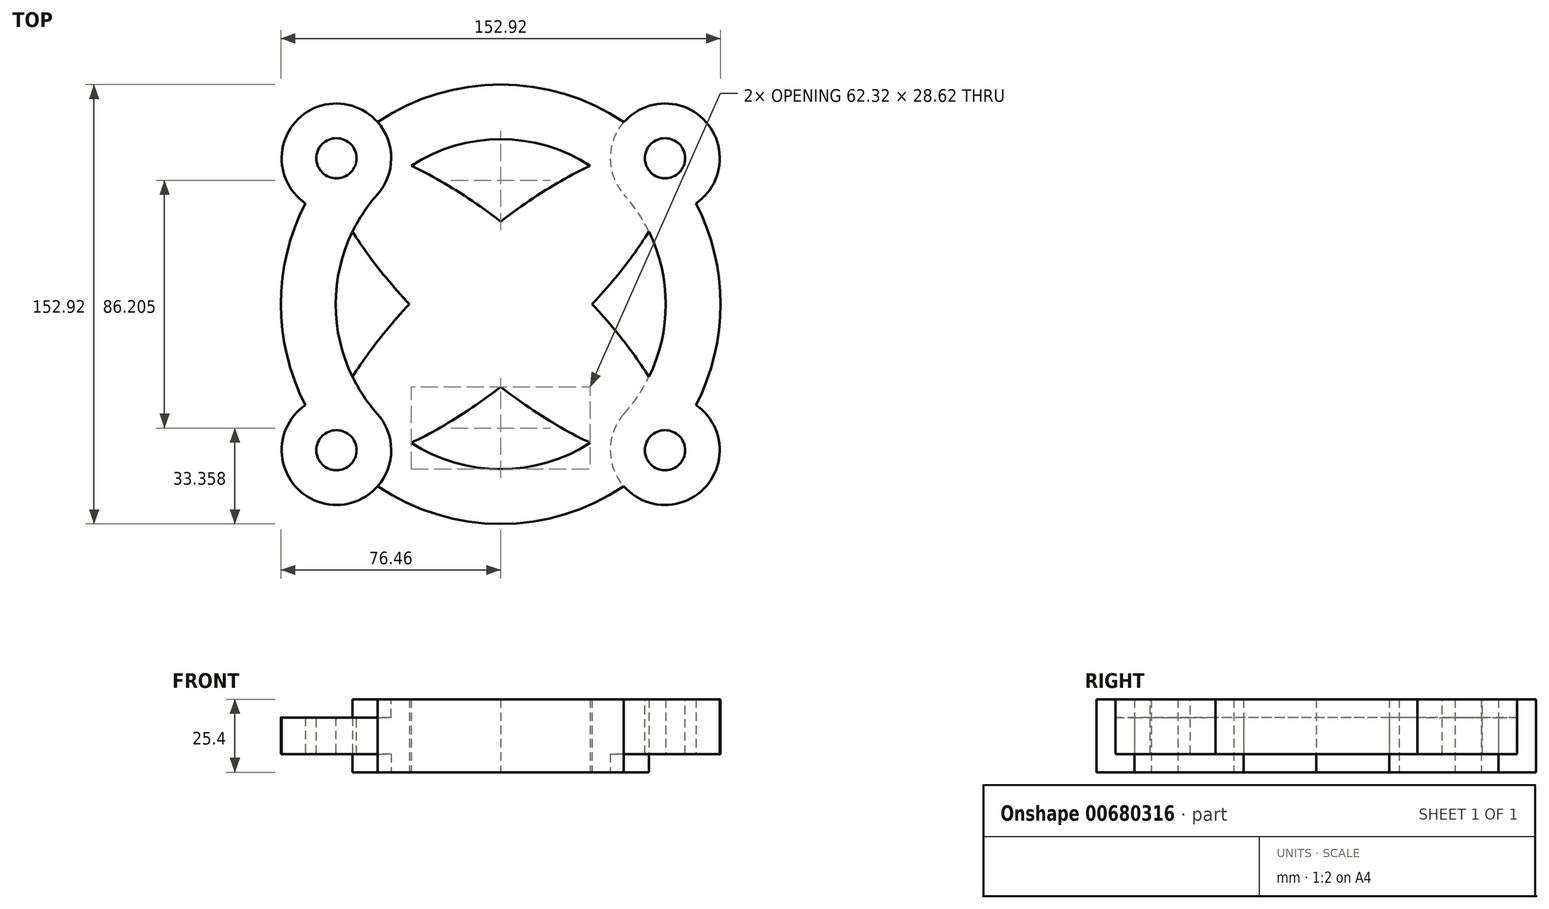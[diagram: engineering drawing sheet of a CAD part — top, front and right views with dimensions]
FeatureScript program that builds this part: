
annotation { "Feature Type Name" : "Feature", "Feature Type Description" : "" }
export const myFeature = defineFeature(function(context is Context, id is Id, definition is map)
    precondition{}
    {
        {
            var Q0;
            Q0=qCreatedBy(makeId("Top.planeOp"),FACE);
            var sketch = newSketch(context, id + "F0", { "sketchPlane" : qUnion([Q0])});
            skLineSegment(sketch, "E0.bottom", {"start": v(76.2, 69.85) * mm, "end": v(-76.2, 69.85) * mm, "construction": true});
            skLineSegment(sketch, "E0.top", {"start": v(76.2, -69.85) * mm, "end": v(-76.2, -69.85) * mm, "construction": true});
            skLineSegment(sketch, "E0.left", {"start": v(76.2, 69.85) * mm, "end": v(76.2, -69.85) * mm, "construction": true});
            skLineSegment(sketch, "E0.right", {"start": v(-76.2, 69.85) * mm, "end": v(-76.2, -69.85) * mm, "construction": true});
            skPoint(sketch, "E0.middle", {"position": v(0, 0) * mm});
            skCircle(sketch, "E1", {"center": v(57.15, 50.8) * mm, "radius": 19.05 * mm});
            skCircle(sketch, "E2", {"center": v(-57.15, 50.8) * mm, "radius": 19.05 * mm});
            skCircle(sketch, "E3", {"center": v(57.15, -50.8) * mm, "radius": 19.05 * mm});
            skCircle(sketch, "E4", {"center": v(-57.15, -50.8) * mm, "radius": 19.05 * mm});
            skEllipse(sketch, "E5", {"center": v(0, 0) * mm, "majorRadius": 76.46 * mm, "minorRadius": 22.23 * mm, "majorAxis": v(0.75, 0.66)});
            skEllipse(sketch, "E6", {"center": v(0, 0) * mm, "majorRadius": 76.46 * mm, "minorRadius": 22.23 * mm, "majorAxis": v(0.75, -0.66)});
            skLineSegment(sketch, "E7", {"start": v(-57.15, 50.8) * mm, "end": v(57.15, -50.8) * mm, "construction": true});
            skLineSegment(sketch, "E8", {"start": v(57.15, 50.8) * mm, "end": v(-57.15, -50.8) * mm, "construction": true});
            skCircle(sketch, "E9", {"center": v(0, 0) * mm, "radius": 76.46 * mm});
            skCircle(sketch, "E10", {"center": v(0, 0) * mm, "radius": 57.41 * mm});
            skSolve(sketch);
        }
        {
            var Q0;
            {var subQ0=sQuery(id+"F0.wireOp",EDGE,"E9");var subQ1=sQuery(id+"F0.wireOp",EDGE,"E2");var subQ2=makeQuery(id+"F0.imprint","INTERSECT",VERTEX,{"disambiguationData":[OD(0.0)],"derivedFrom":[subQ1,subQ0]});Q0=makeQuery(id+"F0.imprint","IMPRINT",FACE,{"disambiguationData":[TD([[makeQuery(id+"F0.imprint","IMPRINT",EDGE,{"disambiguationData":[TD([[subQ2,-1.0]])],"derivedFrom":subQ1}),1.0]])]});}
            var Q1;
            {var subQ5=sQuery(id+"F0.wireOp",EDGE,"E9");var subQ6=sQuery(id+"F0.wireOp",EDGE,"E1");var subQ7=makeQuery(id+"F0.imprint","INTERSECT",VERTEX,{"disambiguationData":[OD(0.0)],"derivedFrom":[subQ6,subQ5]});Q1=makeQuery(id+"F0.imprint","IMPRINT",FACE,{"disambiguationData":[TD([[makeQuery(id+"F0.imprint","IMPRINT",EDGE,{"disambiguationData":[TD([[subQ7,-1.0]])],"derivedFrom":subQ6}),-1.0]])]});}
            var Q2;
            {var subQ0=sQuery(id+"F0.wireOp",EDGE,"E9");var subQ1=sQuery(id+"F0.wireOp",EDGE,"E1");var subQ2=makeQuery(id+"F0.imprint","INTERSECT",VERTEX,{"disambiguationData":[OD(0.0)],"derivedFrom":[subQ1,subQ0]});Q2=makeQuery(id+"F0.imprint","IMPRINT",FACE,{"disambiguationData":[TD([[makeQuery(id+"F0.imprint","IMPRINT",EDGE,{"disambiguationData":[TD([[subQ2,1.0]])],"derivedFrom":subQ1}),1.0]])]});}
            var Q3;
            {var subQ0=sQuery(id+"F0.wireOp",EDGE,"E9");var subQ1=sQuery(id+"F0.wireOp",EDGE,"E1");var subQ2=makeQuery(id+"F0.imprint","INTERSECT",VERTEX,{"disambiguationData":[OD(1.0)],"derivedFrom":[subQ1,subQ0]});Q3=makeQuery(id+"F0.imprint","IMPRINT",FACE,{"disambiguationData":[TD([[makeQuery(id+"F0.imprint","IMPRINT",EDGE,{"disambiguationData":[TD([[subQ2,1.0]])],"derivedFrom":subQ1}),1.0]])]});}
            var Q4;
            {var subQ0=sQuery(id+"F0.wireOp",EDGE,"E9");var subQ1=sQuery(id+"F0.wireOp",EDGE,"E1");var subQ2=makeQuery(id+"F0.imprint","INTERSECT",VERTEX,{"disambiguationData":[OD(0.0)],"derivedFrom":[subQ1,subQ0]});Q4=makeQuery(id+"F0.imprint","IMPRINT",FACE,{"disambiguationData":[TD([[makeQuery(id+"F0.imprint","IMPRINT",EDGE,{"disambiguationData":[TD([[subQ2,-1.0]])],"derivedFrom":subQ1}),1.0]])]});}
            var Q5;
            {var subQ0=sQuery(id+"F0.wireOp",EDGE,"E5");var subQ1=sQuery(id+"F0.wireOp",EDGE,"E1");var subQ2=makeQuery(id+"F0.imprint","INTERSECT",VERTEX,{"disambiguationData":[OD(0.0)],"derivedFrom":[subQ1,subQ0]});Q5=makeQuery(id+"F0.imprint","IMPRINT",FACE,{"disambiguationData":[TD([[makeQuery(id+"F0.imprint","IMPRINT",EDGE,{"disambiguationData":[TD([[subQ2,-1.0]])],"derivedFrom":subQ1}),-1.0]])]});}
            var Q6;
            {var subQ0=sQuery(id+"F0.wireOp",EDGE,"E9");var subQ1=sQuery(id+"F0.wireOp",EDGE,"E2");var subQ2=makeQuery(id+"F0.imprint","INTERSECT",VERTEX,{"disambiguationData":[OD(0.0)],"derivedFrom":[subQ1,subQ0]});Q6=makeQuery(id+"F0.imprint","IMPRINT",FACE,{"disambiguationData":[TD([[makeQuery(id+"F0.imprint","IMPRINT",EDGE,{"disambiguationData":[TD([[subQ2,1.0]])],"derivedFrom":subQ1}),1.0]])]});}
            var Q7;
            {var subQ0=sQuery(id+"F0.wireOp",EDGE,"E6");var subQ1=sQuery(id+"F0.wireOp",EDGE,"E2");var subQ2=makeQuery(id+"F0.imprint","INTERSECT",VERTEX,{"disambiguationData":[OD(0.0)],"derivedFrom":[subQ1,subQ0]});Q7=makeQuery(id+"F0.imprint","IMPRINT",FACE,{"disambiguationData":[TD([[makeQuery(id+"F0.imprint","IMPRINT",EDGE,{"disambiguationData":[TD([[subQ2,1.0]])],"derivedFrom":subQ1}),-1.0]])]});}
            var Q8;
            {var subQ0=sQuery(id+"F0.wireOp",EDGE,"E6");var subQ1=sQuery(id+"F0.wireOp",EDGE,"E2");var subQ2=makeQuery(id+"F0.imprint","INTERSECT",VERTEX,{"disambiguationData":[OD(1.0)],"derivedFrom":[subQ1,subQ0]});Q8=makeQuery(id+"F0.imprint","IMPRINT",FACE,{"disambiguationData":[TD([[makeQuery(id+"F0.imprint","IMPRINT",EDGE,{"disambiguationData":[TD([[subQ2,-1.0]])],"derivedFrom":subQ1}),1.0]])]});}
            var Q9;
            {var subQ0=sQuery(id+"F0.wireOp",EDGE,"E9");var subQ1=sQuery(id+"F0.wireOp",EDGE,"E2");var subQ2=makeQuery(id+"F0.imprint","INTERSECT",VERTEX,{"disambiguationData":[OD(1.0)],"derivedFrom":[subQ1,subQ0]});Q9=makeQuery(id+"F0.imprint","IMPRINT",FACE,{"disambiguationData":[TD([[makeQuery(id+"F0.imprint","IMPRINT",EDGE,{"disambiguationData":[TD([[subQ2,-1.0]])],"derivedFrom":subQ1}),1.0]])]});}
            var Q10;
            {var subQ0=sQuery(id+"F0.wireOp",EDGE,"E6");var subQ1=sQuery(id+"F0.wireOp",EDGE,"E2");var subQ2=makeQuery(id+"F0.imprint","INTERSECT",VERTEX,{"disambiguationData":[OD(1.0)],"derivedFrom":[subQ1,subQ0]});Q10=makeQuery(id+"F0.imprint","IMPRINT",FACE,{"disambiguationData":[TD([[makeQuery(id+"F0.imprint","IMPRINT",EDGE,{"disambiguationData":[TD([[subQ2,-1.0]])],"derivedFrom":subQ1}),-1.0]])]});}
            var Q11;
            {var subQ5=sQuery(id+"F0.wireOp",EDGE,"E9");var subQ8=sQuery(id+"F0.wireOp",EDGE,"E2");var subQ11=makeQuery(id+"F0.imprint","INTERSECT",VERTEX,{"disambiguationData":[OD(1.0)],"derivedFrom":[subQ8,subQ5]});Q11=makeQuery(id+"F0.imprint","IMPRINT",FACE,{"disambiguationData":[TD([[makeQuery(id+"F0.imprint","IMPRINT",EDGE,{"disambiguationData":[TD([[subQ11,-1.0]])],"derivedFrom":subQ8}),-1.0]])]});}
            var Q12;
            {var subQ0=sQuery(id+"F0.wireOp",EDGE,"E5");var subQ1=sQuery(id+"F0.wireOp",EDGE,"E4");var subQ2=makeQuery(id+"F0.imprint","INTERSECT",VERTEX,{"disambiguationData":[OD(0.0)],"derivedFrom":[subQ1,subQ0]});Q12=makeQuery(id+"F0.imprint","IMPRINT",FACE,{"disambiguationData":[TD([[makeQuery(id+"F0.imprint","IMPRINT",EDGE,{"disambiguationData":[TD([[subQ2,1.0]])],"derivedFrom":subQ1}),1.0]])]});}
            var Q13;
            {var subQ0=sQuery(id+"F0.wireOp",EDGE,"E9");var subQ1=sQuery(id+"F0.wireOp",EDGE,"E4");var subQ2=makeQuery(id+"F0.imprint","INTERSECT",VERTEX,{"disambiguationData":[OD(0.0)],"derivedFrom":[subQ1,subQ0]});Q13=makeQuery(id+"F0.imprint","IMPRINT",FACE,{"disambiguationData":[TD([[makeQuery(id+"F0.imprint","IMPRINT",EDGE,{"disambiguationData":[TD([[subQ2,1.0]])],"derivedFrom":subQ1}),1.0]])]});}
            var Q14;
            {var subQ0=sQuery(id+"F0.wireOp",EDGE,"E9");var subQ1=sQuery(id+"F0.wireOp",EDGE,"E4");var subQ2=makeQuery(id+"F0.imprint","INTERSECT",VERTEX,{"disambiguationData":[OD(0.0)],"derivedFrom":[subQ1,subQ0]});Q14=makeQuery(id+"F0.imprint","IMPRINT",FACE,{"disambiguationData":[TD([[makeQuery(id+"F0.imprint","IMPRINT",EDGE,{"disambiguationData":[TD([[subQ2,-1.0]])],"derivedFrom":subQ1}),1.0]])]});}
            var Q15;
            {var subQ0=sQuery(id+"F0.wireOp",EDGE,"E9");var subQ1=sQuery(id+"F0.wireOp",EDGE,"E4");var subQ2=makeQuery(id+"F0.imprint","INTERSECT",VERTEX,{"disambiguationData":[OD(1.0)],"derivedFrom":[subQ1,subQ0]});Q15=makeQuery(id+"F0.imprint","IMPRINT",FACE,{"disambiguationData":[TD([[makeQuery(id+"F0.imprint","IMPRINT",EDGE,{"disambiguationData":[TD([[subQ2,-1.0]])],"derivedFrom":subQ1}),1.0]])]});}
            var Q16;
            {var subQ0=sQuery(id+"F0.wireOp",EDGE,"E9");var subQ1=sQuery(id+"F0.wireOp",EDGE,"E3");var subQ2=makeQuery(id+"F0.imprint","INTERSECT",VERTEX,{"disambiguationData":[OD(0.0)],"derivedFrom":[subQ1,subQ0]});Q16=makeQuery(id+"F0.imprint","IMPRINT",FACE,{"disambiguationData":[TD([[makeQuery(id+"F0.imprint","IMPRINT",EDGE,{"disambiguationData":[TD([[subQ2,1.0]])],"derivedFrom":subQ1}),1.0]])]});}
            var Q17;
            {var subQ0=sQuery(id+"F0.wireOp",EDGE,"E9");var subQ1=sQuery(id+"F0.wireOp",EDGE,"E3");var subQ2=makeQuery(id+"F0.imprint","INTERSECT",VERTEX,{"disambiguationData":[OD(1.0)],"derivedFrom":[subQ1,subQ0]});Q17=makeQuery(id+"F0.imprint","IMPRINT",FACE,{"disambiguationData":[TD([[makeQuery(id+"F0.imprint","IMPRINT",EDGE,{"disambiguationData":[TD([[subQ2,1.0]])],"derivedFrom":subQ1}),1.0]])]});}
            var Q18;
            {var subQ0=sQuery(id+"F0.wireOp",EDGE,"E6");var subQ1=sQuery(id+"F0.wireOp",EDGE,"E3");var subQ2=makeQuery(id+"F0.imprint","INTERSECT",VERTEX,{"disambiguationData":[OD(0.0)],"derivedFrom":[subQ1,subQ0]});Q18=makeQuery(id+"F0.imprint","IMPRINT",FACE,{"disambiguationData":[TD([[makeQuery(id+"F0.imprint","IMPRINT",EDGE,{"disambiguationData":[TD([[subQ2,-1.0]])],"derivedFrom":subQ1}),1.0]])]});}
            var Q19;
            {var subQ0=sQuery(id+"F0.wireOp",EDGE,"E6");var subQ1=sQuery(id+"F0.wireOp",EDGE,"E3");var subQ2=makeQuery(id+"F0.imprint","INTERSECT",VERTEX,{"disambiguationData":[OD(0.0)],"derivedFrom":[subQ1,subQ0]});Q19=makeQuery(id+"F0.imprint","IMPRINT",FACE,{"disambiguationData":[TD([[makeQuery(id+"F0.imprint","IMPRINT",EDGE,{"disambiguationData":[TD([[subQ2,-1.0]])],"derivedFrom":subQ1}),-1.0]])]});}
            var Q20;
            {var subQ1=sQuery(id+"F0.wireOp",EDGE,"E1");var subQ5=sQuery(id+"F0.wireOp",EDGE,"E9");var subQ11=makeQuery(id+"F0.imprint","INTERSECT",VERTEX,{"disambiguationData":[OD(1.0)],"derivedFrom":[subQ1,subQ5]});Q20=makeQuery(id+"F0.imprint","IMPRINT",FACE,{"disambiguationData":[TD([[makeQuery(id+"F0.imprint","IMPRINT",EDGE,{"disambiguationData":[TD([[subQ11,1.0]])],"derivedFrom":subQ1}),-1.0]])]});}
            var Q21;
            {var subQ0=sQuery(id+"F0.wireOp",EDGE,"E9");var subQ1=sQuery(id+"F0.wireOp",EDGE,"E3");var subQ2=makeQuery(id+"F0.imprint","INTERSECT",VERTEX,{"disambiguationData":[OD(0.0)],"derivedFrom":[subQ1,subQ0]});Q21=makeQuery(id+"F0.imprint","IMPRINT",FACE,{"disambiguationData":[TD([[makeQuery(id+"F0.imprint","IMPRINT",EDGE,{"disambiguationData":[TD([[subQ2,-1.0]])],"derivedFrom":subQ1}),1.0]])]});}
            var Q22;
            {var subQ0=sQuery(id+"F0.wireOp",EDGE,"E5");var subQ1=sQuery(id+"F0.wireOp",EDGE,"E1");var subQ2=makeQuery(id+"F0.imprint","INTERSECT",VERTEX,{"disambiguationData":[OD(0.0)],"derivedFrom":[subQ1,subQ0]});Q22=makeQuery(id+"F0.imprint","IMPRINT",FACE,{"disambiguationData":[TD([[makeQuery(id+"F0.imprint","IMPRINT",EDGE,{"disambiguationData":[TD([[subQ2,-1.0]])],"derivedFrom":subQ1}),1.0]])]});}
            var Q23;
            {var subQ0=sQuery(id+"F0.wireOp",EDGE,"E10");var subQ1=sQuery(id+"F0.wireOp",EDGE,"E1");var subQ2=makeQuery(id+"F0.imprint","INTERSECT",VERTEX,{"derivedFrom":[subQ1,subQ0]});Q23=makeQuery(id+"F0.imprint","IMPRINT",FACE,{"disambiguationData":[TD([[makeQuery(id+"F0.imprint","IMPRINT",EDGE,{"disambiguationData":[TD([[subQ2,-1.0]])],"derivedFrom":subQ1}),-1.0]])]});}
            var Q24;
            {var subQ1=sQuery(id+"F0.wireOp",EDGE,"E3");var subQ5=sQuery(id+"F0.wireOp",EDGE,"E9");var subQ6=makeQuery(id+"F0.imprint","INTERSECT",VERTEX,{"disambiguationData":[OD(1.0)],"derivedFrom":[subQ1,subQ5]});Q24=makeQuery(id+"F0.imprint","IMPRINT",FACE,{"disambiguationData":[TD([[makeQuery(id+"F0.imprint","IMPRINT",EDGE,{"disambiguationData":[TD([[subQ6,1.0]])],"derivedFrom":subQ1}),-1.0]])]});}
            var Q25;
            {var subQ0=sQuery(id+"F0.wireOp",EDGE,"E10");var subQ1=sQuery(id+"F0.wireOp",EDGE,"E3");var subQ2=makeQuery(id+"F0.imprint","INTERSECT",VERTEX,{"derivedFrom":[subQ1,subQ0]});Q25=makeQuery(id+"F0.imprint","IMPRINT",FACE,{"disambiguationData":[TD([[makeQuery(id+"F0.imprint","IMPRINT",EDGE,{"disambiguationData":[TD([[subQ2,-1.0]])],"derivedFrom":subQ1}),-1.0]])]});}
            var Q26;
            {var subQ0=sQuery(id+"F0.wireOp",EDGE,"E10");var subQ1=sQuery(id+"F0.wireOp",EDGE,"E4");var subQ2=makeQuery(id+"F0.imprint","INTERSECT",VERTEX,{"derivedFrom":[subQ1,subQ0]});Q26=makeQuery(id+"F0.imprint","IMPRINT",FACE,{"disambiguationData":[TD([[makeQuery(id+"F0.imprint","IMPRINT",EDGE,{"disambiguationData":[TD([[subQ2,1.0]])],"derivedFrom":subQ1}),-1.0]])]});}
            var Q27;
            {var subQ0=sQuery(id+"F0.wireOp",EDGE,"E5");var subQ1=sQuery(id+"F0.wireOp",EDGE,"E4");var subQ2=makeQuery(id+"F0.imprint","INTERSECT",VERTEX,{"disambiguationData":[OD(0.0)],"derivedFrom":[subQ1,subQ0]});Q27=makeQuery(id+"F0.imprint","IMPRINT",FACE,{"disambiguationData":[TD([[makeQuery(id+"F0.imprint","IMPRINT",EDGE,{"disambiguationData":[TD([[subQ2,1.0]])],"derivedFrom":subQ1}),-1.0]])]});}
            var Q28;
            {var subQ2=sQuery(id+"F0.wireOp",EDGE,"E6");var subQ4=sQuery(id+"F0.wireOp",EDGE,"E5");var subQ7=makeQuery(id+"F0.imprint","INTERSECT",VERTEX,{"disambiguationData":[OD(0.0)],"derivedFrom":[subQ4,subQ2]});Q28=makeQuery(id+"F0.imprint","IMPRINT",FACE,{"disambiguationData":[TD([[makeQuery(id+"F0.imprint","IMPRINT",EDGE,{"disambiguationData":[TD([[subQ7,-1.0]])],"derivedFrom":subQ4}),-1.0]])]});}
            var Q29;
            {var subQ0=sQuery(id+"F0.wireOp",EDGE,"E6");var subQ1=sQuery(id+"F0.wireOp",EDGE,"E5");var subQ2=makeQuery(id+"F0.imprint","INTERSECT",VERTEX,{"disambiguationData":[OD(0.0)],"derivedFrom":[subQ1,subQ0]});Q29=makeQuery(id+"F0.imprint","IMPRINT",FACE,{"disambiguationData":[TD([[makeQuery(id+"F0.imprint","IMPRINT",EDGE,{"disambiguationData":[TD([[subQ2,-1.0]])],"derivedFrom":subQ1}),1.0]])]});}
            var Q30;
            {var subQ2=sQuery(id+"F0.wireOp",EDGE,"E6");var subQ4=sQuery(id+"F0.wireOp",EDGE,"E5");var subQ7=makeQuery(id+"F0.imprint","INTERSECT",VERTEX,{"disambiguationData":[OD(2.0)],"derivedFrom":[subQ4,subQ2]});Q30=makeQuery(id+"F0.imprint","IMPRINT",FACE,{"disambiguationData":[TD([[makeQuery(id+"F0.imprint","IMPRINT",EDGE,{"disambiguationData":[TD([[subQ7,-1.0]])],"derivedFrom":subQ4}),-1.0]])]});}
            var Q31;
            {var subQ0=sQuery(id+"F0.wireOp",EDGE,"E10");var subQ2=sQuery(id+"F0.wireOp",EDGE,"E5");var subQ7=makeQuery(id+"F0.imprint","INTERSECT",VERTEX,{"disambiguationData":[OD(0.0)],"derivedFrom":[subQ2,subQ0]});Q31=makeQuery(id+"F0.imprint","IMPRINT",FACE,{"disambiguationData":[TD([[makeQuery(id+"F0.imprint","IMPRINT",EDGE,{"disambiguationData":[TD([[subQ7,-1.0]])],"derivedFrom":subQ2}),1.0]])]});}
            var Q32;
            {var subQ2=sQuery(id+"F0.wireOp",EDGE,"E5");var subQ4=sQuery(id+"F0.wireOp",EDGE,"E6");var subQ5=makeQuery(id+"F0.imprint","INTERSECT",VERTEX,{"disambiguationData":[OD(1.0)],"derivedFrom":[subQ2,subQ4]});Q32=makeQuery(id+"F0.imprint","IMPRINT",FACE,{"disambiguationData":[TD([[makeQuery(id+"F0.imprint","IMPRINT",EDGE,{"disambiguationData":[TD([[subQ5,-1.0]])],"derivedFrom":subQ2}),1.0]])]});}
            extrude(context, id + "F1", {"entities" : qUnion([Q0, Q1, Q2, Q3, Q4, Q5, Q6, Q7, Q8, Q9, Q10, Q11, Q12, Q13, Q14, Q15, Q16, Q17, Q18, Q19, Q20, Q21, Q22, Q23, Q24, Q25, Q26, Q27, Q28, Q29, Q30, Q31, Q32]), "depth" : 25.4 * mm, "offsetDistance" : 25.4 * mm});
        }
        {
            var Q0;
            Q0=makeQuery(id+"F1.opExtrude","CAP_FACE",FACE,{"disambiguationData":[OSD([sQuery(id+"F0.wireOp",EDGE,"E1"),sQuery(id+"F0.wireOp",EDGE,"E2"),sQuery(id+"F0.wireOp",EDGE,"E3"),sQuery(id+"F0.wireOp",EDGE,"E4"),sQuery(id+"F0.wireOp",EDGE,"E5"),sQuery(id+"F0.wireOp",EDGE,"E6"),sQuery(id+"F0.wireOp",EDGE,"E9"),sQuery(id+"F0.wireOp",EDGE,"E10")])],"isStart":false});
            var sketch = newSketch(context, id + "F2", { "sketchPlane" : qUnion([Q0])});
            skCircle(sketch, "E11", {"center": v(-57.15, 50.8) * mm, "radius": 6.99 * mm});
            skCircle(sketch, "E12", {"center": v(-57.15, -50.8) * mm, "radius": 6.99 * mm});
            skCircle(sketch, "E13", {"center": v(57.15, -50.8) * mm, "radius": 6.99 * mm});
            skCircle(sketch, "E14", {"center": v(57.15, 50.8) * mm, "radius": 6.99 * mm});
            skSolve(sketch);
        }
        {
            var Q0;
            Q0 = qSketchRegion(id + "F2", true);
            extrude(context, id + "F3", {"entities" : qUnion([Q0]), "operationType" : NewBodyOperationType.REMOVE, "oppositeDirection" : true, "depth" : 25.4 * mm, "offsetDistance" : 25.4 * mm});
        }
        {
            var Q0;
            Q0=makeQuery(id+"F1.opExtrude","CAP_FACE",FACE,{"disambiguationData":[OSD([sQuery(id+"F0.wireOp",EDGE,"E1"),sQuery(id+"F0.wireOp",EDGE,"E2"),sQuery(id+"F0.wireOp",EDGE,"E3"),sQuery(id+"F0.wireOp",EDGE,"E4"),sQuery(id+"F0.wireOp",EDGE,"E5"),sQuery(id+"F0.wireOp",EDGE,"E6"),sQuery(id+"F0.wireOp",EDGE,"E9"),sQuery(id+"F0.wireOp",EDGE,"E10")])],"isStart":false});
            var sketch = newSketch(context, id + "F4", { "sketchPlane" : qUnion([Q0])});
            skArc(sketch, "E15.0", {"start": v(-42.91, 38.14) * mm, "mid": v(-59.45, 69.71) * mm, "end": v(-67.93, 35.1) * mm});
            skArc(sketch, "E16.0", {"start": v(-67.93, -35.1) * mm, "mid": v(-59.45, -69.71) * mm, "end": v(-42.91, -38.14) * mm});
            skArc(sketch, "E17.0", {"start": v(67.93, 35.1) * mm, "mid": v(59.45, 69.71) * mm, "end": v(42.91, 38.14) * mm});
            skArc(sketch, "E18.0", {"start": v(42.91, -38.14) * mm, "mid": v(59.45, -69.71) * mm, "end": v(67.93, -35.1) * mm});
            skArc(sketch, "E19.0", {"start": v(-42.91, 38.14) * mm, "mid": v(-57.41, 0) * mm, "end": v(-42.91, -38.14) * mm});
            skLineSegment(sketch, "E20.0", {"start": v(76.2, 69.85) * mm, "end": v(76.2, -69.85) * mm});
            skArc(sketch, "E21.0", {"start": v(-67.93, 35.1) * mm, "mid": v(-76.46, 0) * mm, "end": v(-67.93, -35.1) * mm});
            skArc(sketch, "E22.trimOffspring", {"start": v(42.91, -38.14) * mm, "mid": v(57.41, 0) * mm, "end": v(42.91, 38.14) * mm});
            skArc(sketch, "E23.trimOffspring", {"start": v(67.93, -35.1) * mm, "mid": v(76.46, 0) * mm, "end": v(67.93, 35.1) * mm});
            skSolve(sketch);
        }
        {
            var Q0;
            {var subQ0=sQuery(id+"F4.wireOp",EDGE,"E23.trimOffspring");var subQ1=sQuery(id+"F4.wireOp",EDGE,"E20.0");var subQ2=makeQuery(id+"F4.imprint","INTERSECT",VERTEX,{"disambiguationData":[OD(0.0)],"derivedFrom":[subQ1,subQ0]});Q0=makeQuery(id+"F4.imprint","IMPRINT",FACE,{"disambiguationData":[TD([[makeQuery(id+"F4.imprint","IMPRINT",EDGE,{"disambiguationData":[TD([[subQ2,-1.0]])],"derivedFrom":subQ1}),1.0]])]});}
            var Q1;
            Q1=makeQuery(id+"F4.imprint","IMPRINT",FACE,{"disambiguationData":[TD([[makeQuery(id+"F4.imprint","IMPRINT",EDGE,{"derivedFrom":makeQuery(id+"F3.boolean.opBoolean","COPY",EDGE,{"derivedFrom":makeQuery(id+"F3.opExtrude","CAP_EDGE",EDGE,{"disambiguationData":[OSD([sQuery(id+"F2.wireOp",EDGE,"E11")])],"isStart":true})})}),1.0]])]});
            var Q2;
            Q2=makeQuery(id+"F4.imprint","IMPRINT",FACE,{"disambiguationData":[TD([[makeQuery(id+"F4.imprint","IMPRINT",EDGE,{"derivedFrom":makeQuery(id+"F3.boolean.opBoolean","COPY",EDGE,{"derivedFrom":makeQuery(id+"F3.opExtrude","CAP_EDGE",EDGE,{"disambiguationData":[OSD([sQuery(id+"F2.wireOp",EDGE,"E12")])],"isStart":true})})}),1.0]])]});
            var Q3;
            Q3=makeQuery(id+"F4.imprint","IMPRINT",FACE,{"disambiguationData":[TD([[makeQuery(id+"F4.imprint","IMPRINT",EDGE,{"derivedFrom":makeQuery(id+"F3.boolean.opBoolean","COPY",EDGE,{"derivedFrom":makeQuery(id+"F3.opExtrude","CAP_EDGE",EDGE,{"disambiguationData":[OSD([sQuery(id+"F2.wireOp",EDGE,"E13")])],"isStart":true})})}),1.0]])]});
            var Q4;
            Q4=makeQuery(id+"F4.imprint","IMPRINT",FACE,{"disambiguationData":[TD([[makeQuery(id+"F4.imprint","IMPRINT",EDGE,{"derivedFrom":makeQuery(id+"F3.boolean.opBoolean","COPY",EDGE,{"derivedFrom":makeQuery(id+"F3.opExtrude","CAP_EDGE",EDGE,{"disambiguationData":[OSD([sQuery(id+"F2.wireOp",EDGE,"E14")])],"isStart":true})})}),1.0]])]});
            var Q5;
            {var subQ5=sQuery(id+"F4.wireOp",EDGE,"E21.0");Q5=makeQuery(id+"F4.imprint","IMPRINT",FACE,{"disambiguationData":[TD([[makeQuery(id+"F4.imprint","IMPRINT",EDGE,{"derivedFrom":subQ5}),1.0]])]});}
            var Q6;
            Q6=makeQuery(id+"F4.imprint","IMPRINT",FACE,{"disambiguationData":[TD([[makeQuery(id+"F4.imprint","IMPRINT",EDGE,{"derivedFrom":makeQuery(id+"F3.boolean.opBoolean","COPY",EDGE,{"derivedFrom":makeQuery(id+"F3.opExtrude","CAP_EDGE",EDGE,{"disambiguationData":[OSD([sQuery(id+"F2.wireOp",EDGE,"E13")])],"isStart":true})})}),-1.0]])]});
            extrude(context, id + "F5", {"entities" : qUnion([Q0, Q1, Q2, Q3, Q4, Q5, Q6]), "operationType" : NewBodyOperationType.REMOVE, "oppositeDirection" : true, "depth" : 6.35 * mm, "offsetDistance" : 25.4 * mm});
        }
        {
            var Q0;
            {var subQ2=sQuery(id+"F0.wireOp",EDGE,"E6");var subQ4=sQuery(id+"F0.wireOp",EDGE,"E5");var subQ7=makeQuery(id+"F0.imprint","INTERSECT",VERTEX,{"disambiguationData":[OD(0.0)],"derivedFrom":[subQ4,subQ2]});Q0=makeQuery(id+"F0.imprint","IMPRINT",FACE,{"disambiguationData":[TD([[makeQuery(id+"F0.imprint","IMPRINT",EDGE,{"disambiguationData":[TD([[subQ7,-1.0]])],"derivedFrom":subQ4}),-1.0]])]});}
            var sketch = newSketch(context, id + "F6", { "sketchPlane" : qUnion([Q0])});
            skArc(sketch, "E24.0.0", {"start": v(-51.54, 25.3) * mm, "mid": v(-47.66, 32) * mm, "end": v(-42.91, 38.14) * mm});
            skArc(sketch, "E24.0.1", {"start": v(-42.91, 38.14) * mm, "mid": v(-38.1, 50.73) * mm, "end": v(-42.82, 63.35) * mm});
            skArc(sketch, "E24.0.2", {"start": v(-42.82, 63.35) * mm, "mid": v(-71.39, 63.46) * mm, "end": v(-67.93, 35.1) * mm});
            skArc(sketch, "E24.0.3", {"start": v(-67.93, 35.1) * mm, "mid": v(-76.46, 0) * mm, "end": v(-67.93, -35.1) * mm});
            skArc(sketch, "E24.0.4", {"start": v(-67.93, -35.1) * mm, "mid": v(-71.39, -63.46) * mm, "end": v(-42.82, -63.35) * mm});
            skArc(sketch, "E24.0.5", {"start": v(-42.82, -63.35) * mm, "mid": v(-38.1, -50.73) * mm, "end": v(-42.91, -38.14) * mm});
            skArc(sketch, "E24.0.6", {"start": v(-42.91, -38.14) * mm, "mid": v(-47.66, -32) * mm, "end": v(-51.54, -25.3) * mm});
            skArc(sketch, "E24.0.7", {"start": v(-51.54, -25.3) * mm, "mid": v(-57.41, 0) * mm, "end": v(-51.54, 25.3) * mm});
            skArc(sketch, "E25.0.0", {"start": v(67.93, -35.1) * mm, "mid": v(76.46, 0) * mm, "end": v(67.93, 35.1) * mm});
            skArc(sketch, "E25.0.1", {"start": v(67.93, 35.1) * mm, "mid": v(71.39, 63.46) * mm, "end": v(42.82, 63.35) * mm});
            skArc(sketch, "E25.0.2", {"start": v(42.82, 63.35) * mm, "mid": v(38.1, 50.73) * mm, "end": v(42.91, 38.14) * mm});
            skArc(sketch, "E25.0.3", {"start": v(42.91, 38.14) * mm, "mid": v(47.66, 32) * mm, "end": v(51.54, 25.3) * mm});
            skArc(sketch, "E25.0.4", {"start": v(51.54, 25.3) * mm, "mid": v(57.41, 0) * mm, "end": v(51.54, -25.3) * mm});
            skArc(sketch, "E25.0.5", {"start": v(51.54, -25.3) * mm, "mid": v(47.66, -32) * mm, "end": v(42.91, -38.14) * mm});
            skArc(sketch, "E25.0.6", {"start": v(42.91, -38.14) * mm, "mid": v(38.1, -50.73) * mm, "end": v(42.82, -63.35) * mm});
            skArc(sketch, "E25.0.7", {"start": v(42.82, -63.35) * mm, "mid": v(71.39, -63.46) * mm, "end": v(67.93, -35.1) * mm});
            skSolve(sketch);
        }
        {
            var Q0;
            Q0 = qSketchRegion(id + "F6", true);
            extrude(context, id + "F7", {"entities" : qUnion([Q0]), "operationType" : NewBodyOperationType.REMOVE, "depth" : 6.35 * mm, "offsetDistance" : 25.4 * mm});
        }
    });
